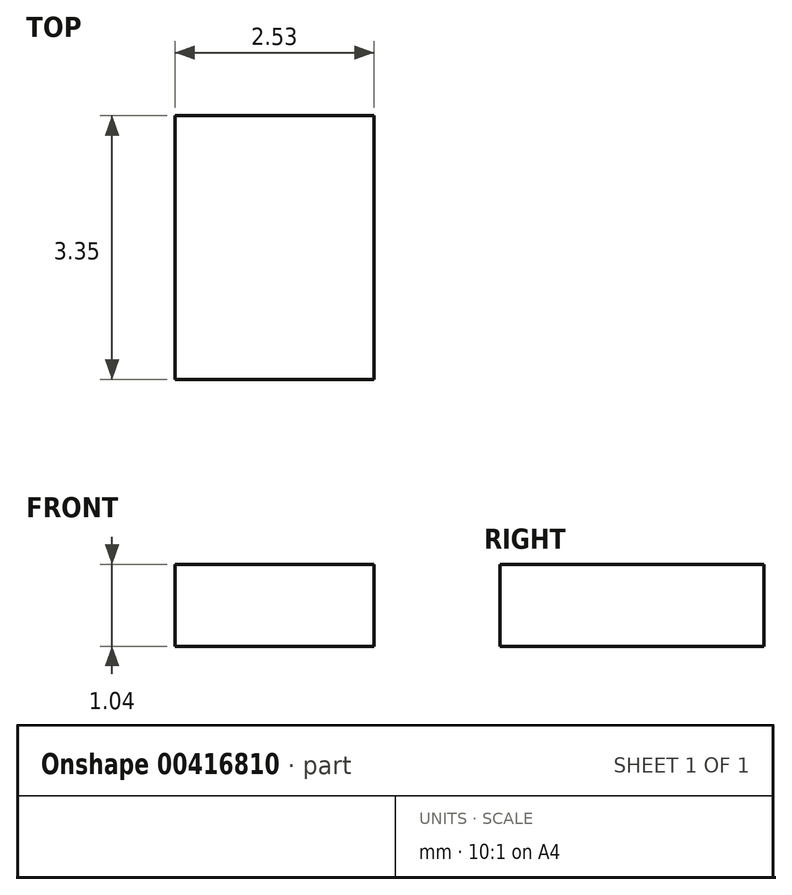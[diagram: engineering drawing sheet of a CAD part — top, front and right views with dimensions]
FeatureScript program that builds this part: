
annotation { "Feature Type Name" : "Feature", "Feature Type Description" : "" }
export const myFeature = defineFeature(function(context is Context, id is Id, definition is map)
    precondition{}
    {
        {
            var Q0;
            Q0=qCreatedBy(makeId("Top.planeOp"),FACE);
            var sketch = newSketch(context, id + "F0", { "sketchPlane" : qUnion([Q0])});
            skLineSegment(sketch, "E0.bottom", {"start": v(0, 0) * mm, "end": v(2.53, 0) * mm});
            skLineSegment(sketch, "E0.top", {"start": v(0, 3.35) * mm, "end": v(2.53, 3.35) * mm});
            skLineSegment(sketch, "E0.left", {"start": v(0, 0) * mm, "end": v(0, 3.35) * mm});
            skLineSegment(sketch, "E0.right", {"start": v(2.53, 0) * mm, "end": v(2.53, 3.35) * mm});
            skSolve(sketch);
        }
        {
            var Q0;
            Q0 = qSketchRegion(id + "F0", true);
            extrude(context, id + "F1", {"entities" : qUnion([Q0]), "depth" : 1.04 * mm, "offsetDistance" : 25.4 * mm});
        }
    });
